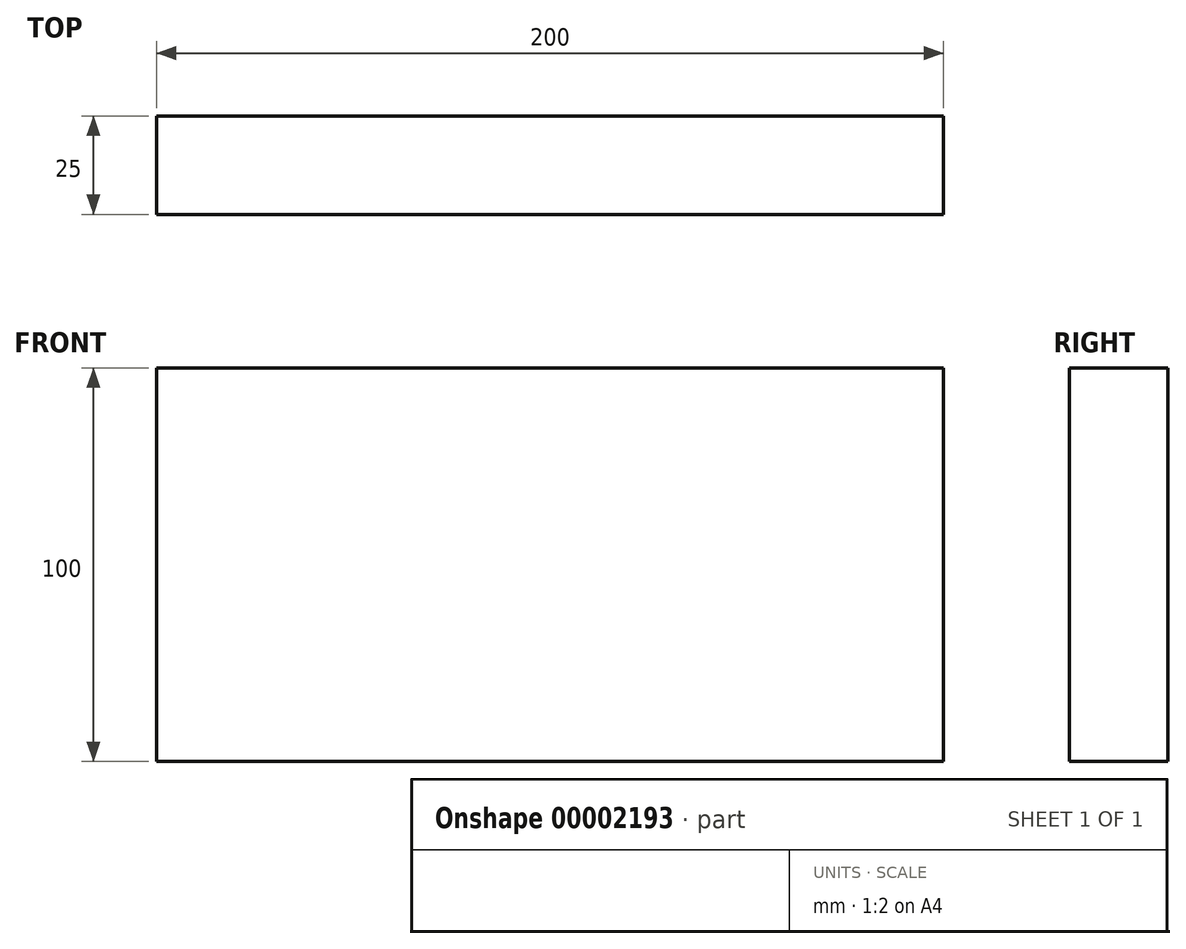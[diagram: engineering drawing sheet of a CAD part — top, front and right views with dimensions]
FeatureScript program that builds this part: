
annotation { "Feature Type Name" : "Feature", "Feature Type Description" : "" }
export const myFeature = defineFeature(function(context is Context, id is Id, definition is map)
    precondition{}
    {
        {
            var Q0;
            Q0=qCreatedBy(makeId("Front.planeOp"),FACE);
            var sketch = newSketch(context, id + "F0", { "sketchPlane" : qUnion([Q0])});
            skLineSegment(sketch, "E0.bottom", {"start": v(0, 0) * mm, "end": v(200, 0) * mm});
            skLineSegment(sketch, "E0.top", {"start": v(0, 100) * mm, "end": v(200, 100) * mm});
            skLineSegment(sketch, "E0.left", {"start": v(0, 0) * mm, "end": v(0, 100) * mm});
            skLineSegment(sketch, "E0.right", {"start": v(200, 0) * mm, "end": v(200, 100) * mm});
            skSolve(sketch);
        }
        {
            var Q0;
            Q0=makeQuery(id+"F0.imprint","IMPRINT",FACE,{"disambiguationData":[TD([[makeQuery(id+"F0.imprint","IMPRINT",EDGE,{"derivedFrom":sQuery(id+"F0.wireOp",EDGE,"E0.bottom")}),1.0]])]});
            extrude(context, id + "F1", {"entities" : qUnion([Q0]), "depth" : 25 * mm});
        }
    });
